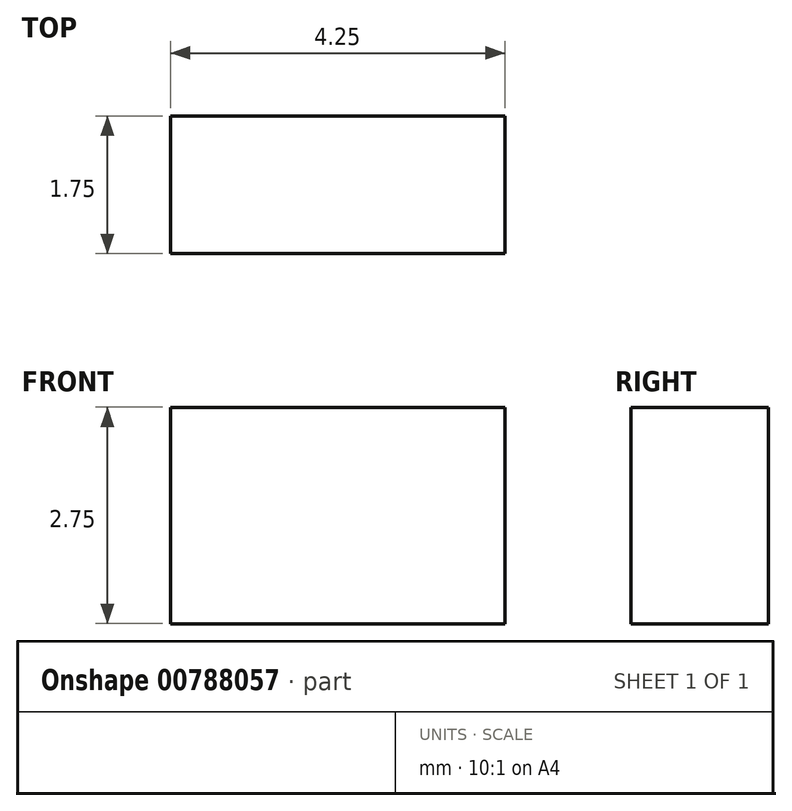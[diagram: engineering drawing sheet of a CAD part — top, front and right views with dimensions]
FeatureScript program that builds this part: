
annotation { "Feature Type Name" : "Feature", "Feature Type Description" : "" }
export const myFeature = defineFeature(function(context is Context, id is Id, definition is map)
    precondition{}
    {
        {
            var Q0;
            Q0=qCreatedBy(makeId("Front.planeOp"),FACE);
            var sketch = newSketch(context, id + "F0", { "sketchPlane" : qUnion([Q0])});
            skLineSegment(sketch, "E0.bottom", {"start": v(4.06, 9.78) * mm, "end": v(8.31, 9.78) * mm});
            skLineSegment(sketch, "E0.top", {"start": v(4.06, 7.03) * mm, "end": v(8.31, 7.03) * mm});
            skLineSegment(sketch, "E0.left", {"start": v(4.06, 9.78) * mm, "end": v(4.06, 7.03) * mm});
            skLineSegment(sketch, "E0.right", {"start": v(8.31, 9.78) * mm, "end": v(8.31, 7.03) * mm});
            skSolve(sketch);
        }
        {
            var Q0;
            Q0=makeQuery(id+"F0.imprint","IMPRINT",FACE,{"disambiguationData":[TD([[makeQuery(id+"F0.imprint","IMPRINT",EDGE,{"derivedFrom":sQuery(id+"F0.wireOp",EDGE,"E0.bottom")}),-1.0]])]});
            extrude(context, id + "F1", {"entities" : qUnion([Q0]), "depth" : 1.75 * mm, "offsetDistance" : 25 * mm});
        }
    });
